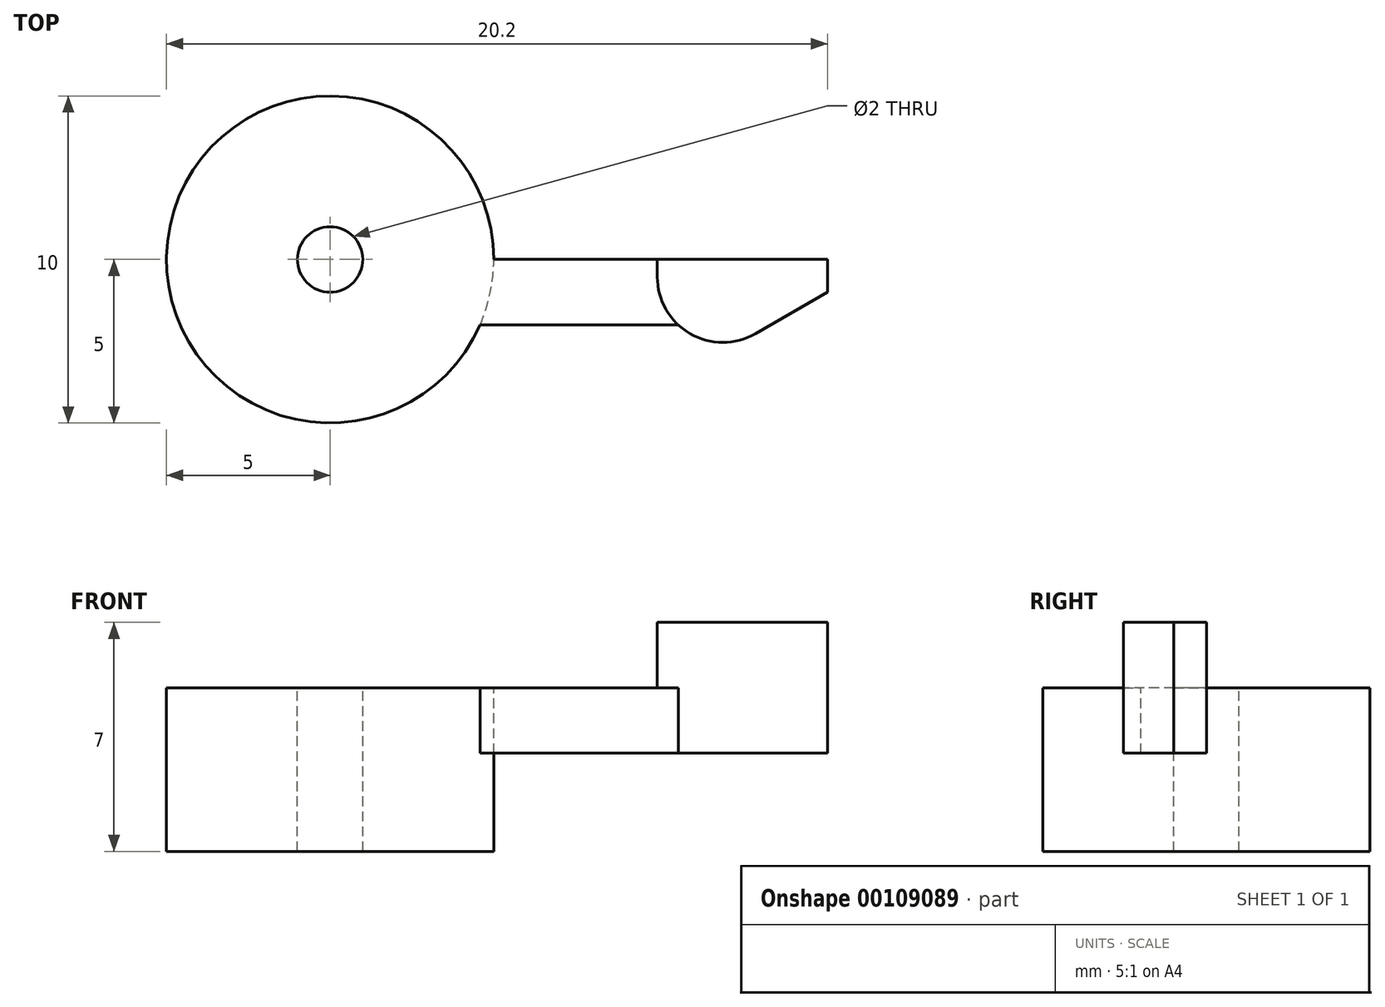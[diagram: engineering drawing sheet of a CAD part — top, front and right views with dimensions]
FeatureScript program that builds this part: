
annotation { "Feature Type Name" : "Feature", "Feature Type Description" : "" }
export const myFeature = defineFeature(function(context is Context, id is Id, definition is map)
    precondition{}
    {
        {
            var Q0;
            Q0=qCreatedBy(makeId("Top.planeOp"),FACE);
            var sketch = newSketch(context, id + "F0", { "sketchPlane" : qUnion([Q0])});
            skCircle(sketch, "E0", {"center": v(0, 0) * mm, "radius": 5 * mm});
            skLineSegment(sketch, "E1", {"start": v(5, 0) * mm, "end": v(10, 0) * mm});
            skLineSegment(sketch, "E2", {"start": v(10, 0) * mm, "end": v(15.2, 0) * mm});
            skLineSegment(sketch, "E3.MirrorCS", {"start": v(10, -2) * mm, "end": v(4.58, -2) * mm});
            skLineSegment(sketch, "E4.MirrorCS", {"start": v(10, 0) * mm, "end": v(10, -2) * mm});
            skLineSegment(sketch, "E5.MirrorCS", {"start": v(10, -2) * mm, "end": v(10, -4) * mm});
            skLineSegment(sketch, "E6.MirrorCS", {"start": v(10, -4) * mm, "end": v(15.2, -1) * mm});
            skLineSegment(sketch, "E7.MirrorCS", {"start": v(15.2, -1) * mm, "end": v(15.2, 0) * mm});
            skLineSegment(sketch, "E8", {"start": v(5, 0) * mm, "end": v(15.2, 0) * mm});
            skSolve(sketch);
        }
        {
            var Q0;
            {var subQ0=sQuery(id+"F0.wireOp",EDGE,"E0");var subQ1=makeQuery(id+"F0.imprint","INTERSECT",VERTEX,{"derivedFrom":[subQ0,sQuery(id+"F0.wireOp",EDGE,"E3.MirrorCS")]});Q0=makeQuery(id+"F0.imprint","IMPRINT",FACE,{"disambiguationData":[TD([[makeQuery(id+"F0.imprint","IMPRINT",EDGE,{"disambiguationData":[TD([[subQ1,1.0]])],"derivedFrom":subQ0}),1.0]])]});}
            extrude(context, id + "F1", {"entities" : qUnion([Q0]), "oppositeDirection" : true, "depth" : 5 * mm});
        }
        {
            var Q0;
            {var subQ0=sQuery(id+"F0.wireOp",EDGE,"E3.MirrorCS");Q0=makeQuery(id+"F0.imprint","IMPRINT",FACE,{"disambiguationData":[TD([[makeQuery(id+"F0.imprint","IMPRINT",EDGE,{"derivedFrom":subQ0}),-1.0]])]});}
            extrude(context, id + "F2", {"entities" : qUnion([Q0]), "operationType" : NewBodyOperationType.ADD, "oppositeDirection" : true, "depth" : 2 * mm});
        }
        {
            var Q0;
            {var subQ1=sQuery(id+"F0.wireOp",EDGE,"E4.MirrorCS");Q0=makeQuery(id+"F0.imprint","IMPRINT",FACE,{"disambiguationData":[TD([[makeQuery(id+"F0.imprint","IMPRINT",EDGE,{"derivedFrom":subQ1}),1.0]])]});}
            extrude(context, id + "F3", {"entities" : qUnion([Q0]), "operationType" : NewBodyOperationType.ADD, "endBound" : BoundingType.SYMMETRIC, "oppositeDirection" : true, "depth" : 4 * mm});
        }
        {
            var Q0;
            Q0=makeQuery(id+"F3.opExtrude","SWEPT_EDGE",EDGE,{"disambiguationData":[OSD([sQuery(id+"F0.wireOp",EDGE,"E5.MirrorCS"),sQuery(id+"F0.wireOp",EDGE,"E6.MirrorCS")])]});
            fillet(context, id + "F4", {"entities" : qUnion([Q0]), "radius" : 2 * mm, "tangentPropagation" : true, "allowEdgeOverflow" : false});
        }
        {
            var Q0;
            Q0=sQuery(id+"F0.wireOp",VERTEX,"E0.center");
            var Q1;
            Q1=makeQuery(id+"F1.opExtrude","SWEPT_BODY",BODY,{"disambiguationData":[OSD([sQuery(id+"F0.wireOp",EDGE,"E0")])]});
            hole(context, id + "F5", {"style" : HoleStyle.SIMPLE, "endStyle" : HoleEndStyle.THROUGH, "holeDiameter" : 2 * mm, "locations" : qUnion([Q0]), "scope" : qUnion([Q1]), "isTappedThrough" : true});
        }
    });
